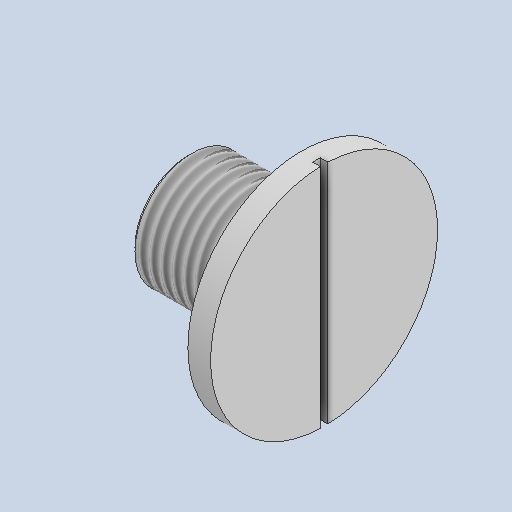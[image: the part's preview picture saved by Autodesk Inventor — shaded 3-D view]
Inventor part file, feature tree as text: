
AUTODESK INVENTOR PART (.ipt)
format: ipt  version: 2023 (Build 270158000, 158)  size: 267,776 bytes
history: native  units: mm
features: sketch x2, other x1, revolve x1, thread x1, chamfer x1, extrude x1
ambient origin geometry x8: Origin, YZ Plane, XZ Plane, XY Plane, X Axis, Y Axis, Z Axis, Center Point
bodies: Body1 (feature_tree)
feature tree (7):
  other  "Твердое тело1"
  revolve  "Вращение1"
  thread  "Резьба1"
  chamfer  "Фаска1"  Distance=15.0mm
  extrude  "Выдавливание1"  Depth=3.0mm
  sketch  "Эскиз1"
  sketch  "Эскиз2"
